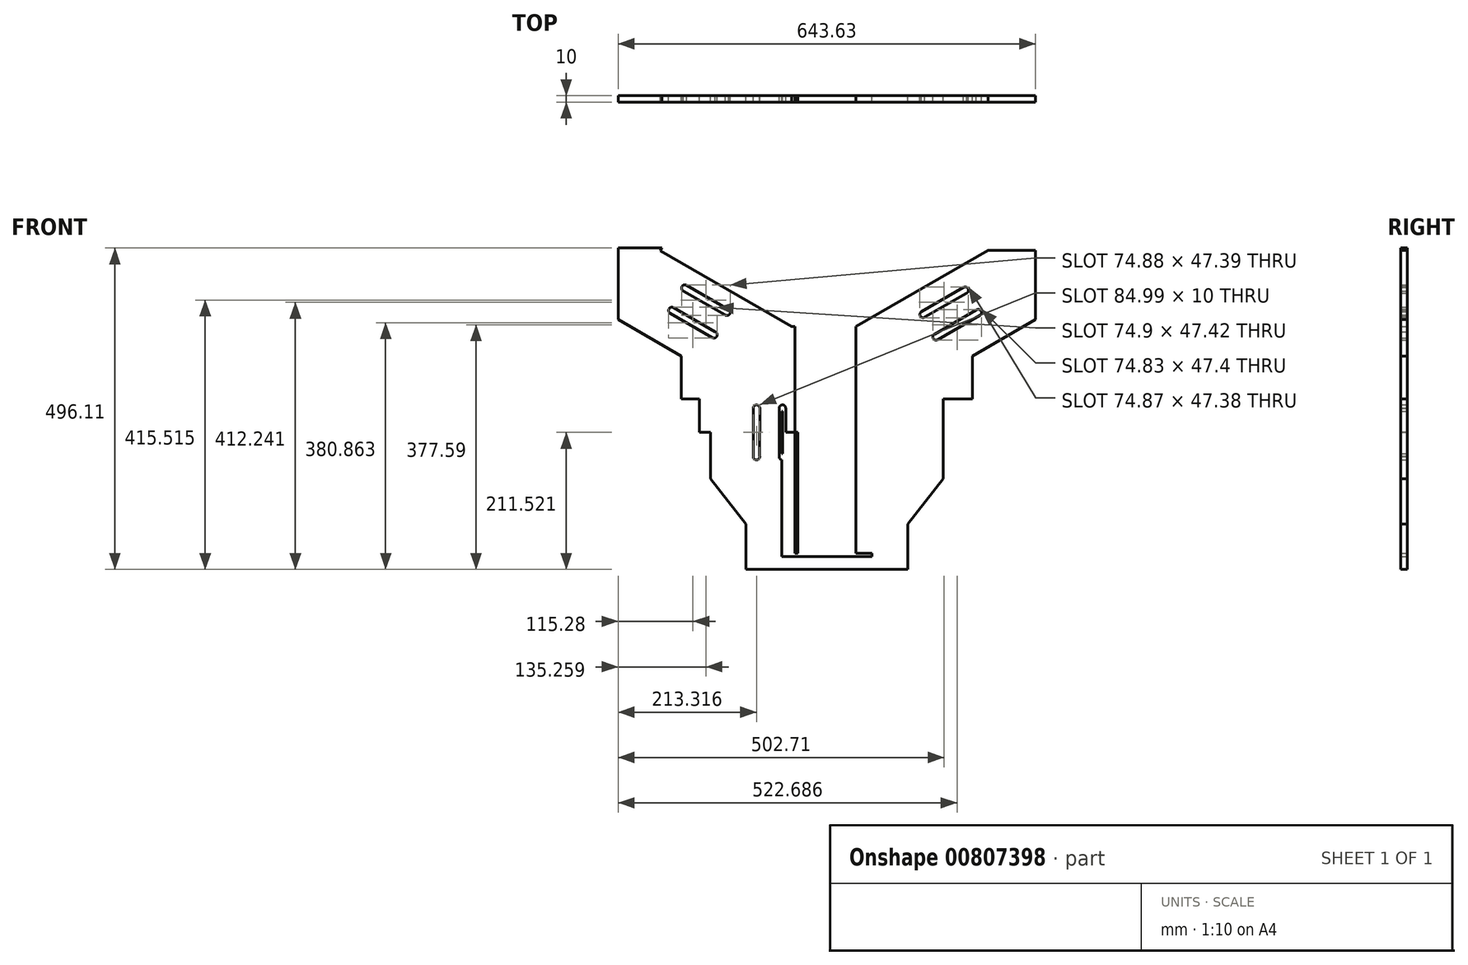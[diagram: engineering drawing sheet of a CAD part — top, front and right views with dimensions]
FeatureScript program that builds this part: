
annotation { "Feature Type Name" : "Feature", "Feature Type Description" : "" }
export const myFeature = defineFeature(function(context is Context, id is Id, definition is map)
    precondition{}
    {
        {
            var Q0;
            Q0=qCreatedBy(makeId("Front.planeOp"),FACE);
            var sketch = newSketch(context, id + "F0", { "sketchPlane" : qUnion([Q0])});
            skLineSegment(sketch, "E0", {"start": v(-67.46, 111.85) * mm, "end": v(-67.46, -238.15) * mm});
            skLineSegment(sketch, "E1", {"start": v(-67.46, -238.15) * mm, "end": v(-42.46, -238.15) * mm});
            skLineSegment(sketch, "E2", {"start": v(-42.46, -238.15) * mm, "end": v(-42.46, 111.85) * mm});
            skLineSegment(sketch, "E3", {"start": v(-42.46, 111.85) * mm, "end": v(-67.46, 111.85) * mm});
            skLineSegment(sketch, "E4", {"start": v(-42.46, 111.85) * mm, "end": v(-345.57, 286.85) * mm});
            skLineSegment(sketch, "E5", {"start": v(-345.57, 286.85) * mm, "end": v(-358.07, 265.2) * mm});
            skLineSegment(sketch, "E6", {"start": v(-358.07, 265.2) * mm, "end": v(-67.46, 97.42) * mm});
            skLineSegment(sketch, "E7", {"start": v(-67.46, -238.15) * mm, "end": v(-67.46, -263.15) * mm});
            skLineSegment(sketch, "E8", {"start": v(-67.46, -263.15) * mm, "end": v(71.54, -263.15) * mm});
            skLineSegment(sketch, "E9", {"start": v(71.54, -263.15) * mm, "end": v(71.54, -238.15) * mm});
            skLineSegment(sketch, "E10", {"start": v(71.54, -238.15) * mm, "end": v(-42.46, -238.15) * mm});
            skLineSegment(sketch, "E11", {"start": v(71.54, -238.15) * mm, "end": v(71.54, 111.85) * mm});
            skLineSegment(sketch, "E12", {"start": v(71.54, 111.85) * mm, "end": v(46.54, 111.85) * mm});
            skLineSegment(sketch, "E13", {"start": v(46.54, 111.85) * mm, "end": v(46.54, -238.15) * mm});
            skLineSegment(sketch, "E14", {"start": v(46.54, 111.85) * mm, "end": v(349.64, 286.85) * mm});
            skLineSegment(sketch, "E15", {"start": v(349.64, 286.85) * mm, "end": v(362.14, 265.2) * mm});
            skLineSegment(sketch, "E16", {"start": v(362.14, 265.2) * mm, "end": v(71.54, 97.42) * mm});
            skLineSegment(sketch, "E17", {"start": v(-345.57, 286.85) * mm, "end": v(-348.07, 282.52) * mm});
            skLineSegment(sketch, "E18", {"start": v(-348.07, 282.52) * mm, "end": v(-52.46, 111.85) * mm});
            skLineSegment(sketch, "E19", {"start": v(-42.46, 111.85) * mm, "end": v(-47.46, 111.85) * mm});
            skLineSegment(sketch, "E20", {"start": v(-47.46, 111.85) * mm, "end": v(-47.46, -238.15) * mm});
            skLineSegment(sketch, "E21", {"start": v(-67.46, -238.15) * mm, "end": v(-67.46, -243.15) * mm});
            skLineSegment(sketch, "E22", {"start": v(-67.46, -243.15) * mm, "end": v(71.54, -243.15) * mm});
            skLineSegment(sketch, "E23", {"start": v(46.54, -238.15) * mm, "end": v(51.54, -238.15) * mm});
            skLineSegment(sketch, "E24", {"start": v(51.54, -238.15) * mm, "end": v(51.54, 111.85) * mm});
            skPoint(sketch, "E24.endSnap0", {"position": v(59.04, 111.85) * mm});
            skLineSegment(sketch, "E25", {"start": v(349.64, 286.85) * mm, "end": v(352.14, 282.52) * mm});
            skLineSegment(sketch, "E26", {"start": v(352.14, 282.52) * mm, "end": v(56.54, 111.85) * mm});
            skLineSegment(sketch, "E27", {"start": v(-191.27, 155.1) * mm, "end": v(-243.23, 185.1) * mm});
            skLineSegment(sketch, "E28", {"start": v(-264.73, 197.63) * mm, "end": v(-319.78, 102.28) * mm});
            skLineSegment(sketch, "E29", {"start": v(-319.78, 102.28) * mm, "end": v(-67.46, -43.4) * mm});
            skLineSegment(sketch, "E30", {"start": v(-67.46, -18.3) * mm, "end": v(-67.46, -38.05) * mm});
            skLineSegment(sketch, "E31", {"start": v(-67.46, -38.05) * mm, "end": v(-67.46, -98.05) * mm});
            skLineSegment(sketch, "E32", {"start": v(-67.46, -123.15) * mm, "end": v(-177.46, -123.15) * mm});
            skLineSegment(sketch, "E33", {"start": v(-177.46, -123.15) * mm, "end": v(-177.46, 20.12) * mm});
            skLineSegment(sketch, "E34", {"start": v(-177.46, -123.15) * mm, "end": v(-67.46, -263.15) * mm});
            skLineSegment(sketch, "E35", {"start": v(71.54, -123.15) * mm, "end": v(181.54, -123.15) * mm});
            skLineSegment(sketch, "E36", {"start": v(181.54, -123.15) * mm, "end": v(71.54, -263.15) * mm});
            skLineSegment(sketch, "E37", {"start": v(181.54, -123.15) * mm, "end": v(181.54, 20.12) * mm});
            skLineSegment(sketch, "E38", {"start": v(71.54, -43.4) * mm, "end": v(181.54, 20.12) * mm});
            skLineSegment(sketch, "E39", {"start": v(181.54, 20.12) * mm, "end": v(323.85, 102.28) * mm});
            skLineSegment(sketch, "E40", {"start": v(323.85, 102.28) * mm, "end": v(262.88, 207.89) * mm});
            skLineSegment(sketch, "E41", {"start": v(-264.73, 211.3) * mm, "end": v(-252.23, 232.96) * mm});
            skLineSegment(sketch, "E42", {"start": v(262.88, 207.89) * mm, "end": v(250.38, 229.54) * mm});
            skLineSegment(sketch, "E43", {"start": v(-319.78, 102.28) * mm, "end": v(-319.78, 232.96) * mm});
            skLineSegment(sketch, "E44", {"start": v(-319.78, 232.96) * mm, "end": v(-252.23, 232.96) * mm});
            skLineSegment(sketch, "E45", {"start": v(250.38, 229.54) * mm, "end": v(323.85, 229.54) * mm});
            skLineSegment(sketch, "E46", {"start": v(323.85, 229.54) * mm, "end": v(323.85, 102.28) * mm});
            skLineSegment(sketch, "E47", {"start": v(-122.46, -193.15) * mm, "end": v(-122.46, -263.15) * mm});
            skLineSegment(sketch, "E48", {"start": v(-122.46, -263.15) * mm, "end": v(-67.46, -263.15) * mm});
            skLineSegment(sketch, "E49", {"start": v(71.54, -263.15) * mm, "end": v(126.54, -263.15) * mm});
            skPoint(sketch, "E49.endSnap0", {"position": v(126.54, -193.15) * mm});
            skLineSegment(sketch, "E50", {"start": v(126.54, -263.15) * mm, "end": v(126.54, -193.15) * mm});
            skLineSegment(sketch, "E51", {"start": v(-172.52, 173.14) * mm, "end": v(-222.52, 86.54) * mm});
            skLineSegment(sketch, "E52", {"start": v(-172.52, 173.14) * mm, "end": v(-183.27, 154.52) * mm});
            skLineSegment(sketch, "E53", {"start": v(-183.27, 154.52) * mm, "end": v(-215.74, 173.27) * mm});
            skLineSegment(sketch, "E54", {"start": v(-215.74, 173.27) * mm, "end": v(-217, 171.1) * mm});
            skLineSegment(sketch, "E55", {"start": v(-217, 171.1) * mm, "end": v(-152.04, 133.6) * mm});
            skCircle(sketch, "E56", {"center": v(-217, 171.1) * mm, "radius": 5 * mm});
            skCircle(sketch, "E57", {"center": v(-152.04, 133.6) * mm, "radius": 5 * mm});
            skLineSegment(sketch, "E58", {"start": v(-149.69, 138.02) * mm, "end": v(-154.4, 129.2) * mm});
            skLineSegment(sketch, "E59", {"start": v(-154.4, 129.2) * mm, "end": v(-219.64, 166.86) * mm});
            skLineSegment(sketch, "E60", {"start": v(-217, 171.1) * mm, "end": v(-237, 136.47) * mm});
            skLineSegment(sketch, "E61", {"start": v(-237, 136.47) * mm, "end": v(-172.04, 98.97) * mm});
            skCircle(sketch, "E62", {"center": v(-237, 136.47) * mm, "radius": 5 * mm});
            skCircle(sketch, "E63", {"center": v(-172.04, 98.97) * mm, "radius": 5 * mm});
            skLineSegment(sketch, "E64", {"start": v(-168.96, 102.9) * mm, "end": v(-234.5, 140.8) * mm});
            skLineSegment(sketch, "E65", {"start": v(-234.5, 140.8) * mm, "end": v(-239.5, 132.14) * mm});
            skLineSegment(sketch, "E66", {"start": v(-239.5, 132.14) * mm, "end": v(-174.54, 94.64) * mm});
            skLineSegment(sketch, "E67", {"start": v(-214.43, 175.4) * mm, "end": v(-149.69, 138.02) * mm});
            skLineSegment(sketch, "E68", {"start": v(-42.46, -51.64) * mm, "end": v(-63.96, -51.64) * mm});
            skLineSegment(sketch, "E69", {"start": v(-63.96, -51.64) * mm, "end": v(-63.96, -14.14) * mm});
            skLineSegment(sketch, "E70", {"start": v(-63.96, -14.14) * mm, "end": v(-66.46, -14.14) * mm});
            skLineSegment(sketch, "E71", {"start": v(-66.46, -14.14) * mm, "end": v(-66.46, -89.14) * mm});
            skCircle(sketch, "E72", {"center": v(-66.46, -14.14) * mm, "radius": 5 * mm});
            skCircle(sketch, "E73", {"center": v(-66.46, -89.14) * mm, "radius": 5 * mm});
            skLineSegment(sketch, "E74", {"start": v(-61.47, -88.97) * mm, "end": v(-71.46, -89.3) * mm});
            skLineSegment(sketch, "E75", {"start": v(-71.46, -89.3) * mm, "end": v(-71.46, -13.97) * mm});
            skLineSegment(sketch, "E76", {"start": v(-66.46, -14.14) * mm, "end": v(-106.46, -14.14) * mm});
            skLineSegment(sketch, "E77", {"start": v(-106.46, -14.14) * mm, "end": v(-106.46, -89.14) * mm});
            skCircle(sketch, "E78", {"center": v(-106.46, -14.14) * mm, "radius": 5 * mm});
            skCircle(sketch, "E79", {"center": v(-106.46, -89.14) * mm, "radius": 5 * mm});
            skLineSegment(sketch, "E80", {"start": v(-101.51, -89.83) * mm, "end": v(-101.46, -14.14) * mm});
            skLineSegment(sketch, "E81", {"start": v(-101.46, -14.14) * mm, "end": v(-111.46, -14.14) * mm});
            skLineSegment(sketch, "E82", {"start": v(-111.46, -14.14) * mm, "end": v(-111.46, -89.14) * mm});
            skLineSegment(sketch, "E83", {"start": v(-61.46, -14.21) * mm, "end": v(-61.47, -88.97) * mm});
            skLineSegment(sketch, "E84", {"start": v(170.93, 169.87) * mm, "end": v(181.68, 151.26) * mm});
            skLineSegment(sketch, "E85", {"start": v(181.68, 151.26) * mm, "end": v(149.2, 132.5) * mm});
            skLineSegment(sketch, "E86", {"start": v(149.2, 132.5) * mm, "end": v(150.45, 130.34) * mm});
            skLineSegment(sketch, "E87", {"start": v(150.45, 130.34) * mm, "end": v(215.4, 167.84) * mm});
            skCircle(sketch, "E88", {"center": v(150.45, 130.34) * mm, "radius": 5 * mm});
            skCircle(sketch, "E89", {"center": v(215.4, 167.84) * mm, "radius": 5 * mm});
            skLineSegment(sketch, "E90", {"start": v(212.76, 172.08) * mm, "end": v(218.05, 163.6) * mm});
            skLineSegment(sketch, "E91", {"start": v(218.05, 163.6) * mm, "end": v(152.8, 125.93) * mm});
            skLineSegment(sketch, "E92", {"start": v(150.45, 130.34) * mm, "end": v(170.45, 95.7) * mm});
            skLineSegment(sketch, "E93", {"start": v(170.45, 95.7) * mm, "end": v(235.4, 133.2) * mm});
            skCircle(sketch, "E94", {"center": v(170.45, 95.7) * mm, "radius": 5 * mm});
            skCircle(sketch, "E95", {"center": v(235.4, 133.2) * mm, "radius": 5 * mm});
            skLineSegment(sketch, "E96", {"start": v(233.53, 137.84) * mm, "end": v(167.95, 100.03) * mm});
            skLineSegment(sketch, "E97", {"start": v(167.95, 100.03) * mm, "end": v(172.95, 91.37) * mm});
            skLineSegment(sketch, "E98", {"start": v(172.95, 91.37) * mm, "end": v(237.9, 128.87) * mm});
            skLineSegment(sketch, "E99", {"start": v(148.02, 134.7) * mm, "end": v(212.76, 172.08) * mm});
            skLineSegment(sketch, "E100", {"start": v(170.93, 169.87) * mm, "end": v(144.01, 154.34) * mm});
            skLineSegment(sketch, "E101", {"start": v(-172.52, 173.14) * mm, "end": v(-150.87, 160.64) * mm});
            skLineSegment(sketch, "E102", {"start": v(-42.46, -51.64) * mm, "end": v(-42.46, -26.64) * mm});
            skLineSegment(sketch, "E103", {"start": v(-222.52, 86.54) * mm, "end": v(-222.52, 0) * mm});
            skLineSegment(sketch, "E104", {"start": v(-222.52, 0) * mm, "end": v(-177.46, 0) * mm});
            skLineSegment(sketch, "E105", {"start": v(181.54, 0) * mm, "end": v(226.6, 0) * mm});
            skLineSegment(sketch, "E106", {"start": v(226.6, 0) * mm, "end": v(226.6, 46.13) * mm});
            skLineSegment(sketch, "E107", {"start": v(-222.52, 46.13) * mm, "end": v(-222.52, 66.13) * mm});
            skLineSegment(sketch, "E108", {"start": v(226.6, 46.13) * mm, "end": v(226.6, 66.13) * mm});
            skLineSegment(sketch, "E109", {"start": v(226.6, 66.13) * mm, "end": v(323.85, 122.28) * mm});
            skLineSegment(sketch, "E110", {"start": v(-222.52, 66.13) * mm, "end": v(-319.78, 122.28) * mm});
            skLineSegment(sketch, "E111", {"start": v(-177.46, -51.52) * mm, "end": v(-194.72, -51.52) * mm});
            skLineSegment(sketch, "E112", {"start": v(-194.72, -51.52) * mm, "end": v(-194.72, 0) * mm});
            skSolve(sketch);
        }
        {
            var Q0;
            {var subQ0=sQuery(id+"F0.wireOp",EDGE,"E41");var subQ1=sQuery(id+"F0.wireOp",EDGE,"E6");var subQ2=makeQuery(id+"F0.imprint","INTERSECT",VERTEX,{"derivedFrom":[subQ1,subQ0]});Q0=makeQuery(id+"F0.imprint","IMPRINT",FACE,{"disambiguationData":[TD([[makeQuery(id+"F0.imprint","IMPRINT",EDGE,{"disambiguationData":[TD([[subQ2,1.0]])],"derivedFrom":subQ1}),1.0]])]});}
            var Q1;
            {var subQ0=sQuery(id+"F0.wireOp",EDGE,"E19");Q1=makeQuery(id+"F0.imprint","IMPRINT",FACE,{"disambiguationData":[TD([[makeQuery(id+"F0.imprint","IMPRINT",EDGE,{"derivedFrom":subQ0}),-1.0]])]});}
            var Q2;
            {var subQ0=sQuery(id+"F0.wireOp",EDGE,"E6");var subQ3=makeQuery(id+"F0.imprint","IMPRINT",VERTEX,{"derivedFrom":subQ0});Q2=makeQuery(id+"F0.imprint","IMPRINT",FACE,{"disambiguationData":[TD([[makeQuery(id+"F0.imprint","IMPRINT",EDGE,{"disambiguationData":[TD([[subQ3,1.0]])],"derivedFrom":subQ0}),1.0]])]});}
            var Q3;
            {var subQ5=sQuery(id+"F0.wireOp",EDGE,"E19");Q3=makeQuery(id+"F0.imprint","IMPRINT",FACE,{"disambiguationData":[TD([[makeQuery(id+"F0.imprint","IMPRINT",EDGE,{"derivedFrom":subQ5}),1.0]])]});}
            var Q4;
            {var subQ1=sQuery(id+"F0.wireOp",EDGE,"E7");Q4=makeQuery(id+"F0.imprint","IMPRINT",FACE,{"disambiguationData":[TD([[makeQuery(id+"F0.imprint","IMPRINT",EDGE,{"derivedFrom":subQ1}),-1.0]])]});}
            var Q5;
            {var subQ1=sQuery(id+"F0.wireOp",EDGE,"E1");var subQ3=sQuery(id+"F0.wireOp",EDGE,"E20");var subQ4=makeQuery(id+"F0.imprint","INTERSECT",VERTEX,{"derivedFrom":[subQ1,subQ3]});Q5=makeQuery(id+"F0.imprint","IMPRINT",FACE,{"disambiguationData":[TD([[makeQuery(id+"F0.imprint","IMPRINT",EDGE,{"disambiguationData":[TD([[subQ4,1.0]])],"derivedFrom":subQ3}),1.0]])]});}
            var Q6;
            {var subQ2=sQuery(id+"F0.wireOp",EDGE,"E47");Q6=makeQuery(id+"F0.imprint","IMPRINT",FACE,{"disambiguationData":[TD([[makeQuery(id+"F0.imprint","IMPRINT",EDGE,{"derivedFrom":subQ2}),1.0]])]});}
            var Q7;
            Q7=makeQuery(id+"F0.imprint","IMPRINT",FACE,{"disambiguationData":[TD([[makeQuery(id+"F0.imprint","IMPRINT",EDGE,{"derivedFrom":sQuery(id+"F0.wireOp",EDGE,"E7")}),1.0]])]});
            var Q8;
            {var subQ8=sQuery(id+"F0.wireOp",EDGE,"E21");Q8=makeQuery(id+"F0.imprint","IMPRINT",FACE,{"disambiguationData":[TD([[makeQuery(id+"F0.imprint","IMPRINT",EDGE,{"derivedFrom":subQ8}),1.0]])]});}
            var Q9;
            {var subQ0=sQuery(id+"F0.wireOp",EDGE,"E49");Q9=makeQuery(id+"F0.imprint","IMPRINT",FACE,{"disambiguationData":[TD([[makeQuery(id+"F0.imprint","IMPRINT",EDGE,{"derivedFrom":subQ0}),1.0]])]});}
            var Q10;
            {var subQ0=sQuery(id+"F0.wireOp",EDGE,"E35");Q10=makeQuery(id+"F0.imprint","IMPRINT",FACE,{"disambiguationData":[TD([[makeQuery(id+"F0.imprint","IMPRINT",EDGE,{"derivedFrom":subQ0}),-1.0]])]});}
            var Q11;
            {var subQ6=sQuery(id+"F0.wireOp",EDGE,"E24");Q11=makeQuery(id+"F0.imprint","IMPRINT",FACE,{"disambiguationData":[TD([[makeQuery(id+"F0.imprint","IMPRINT",EDGE,{"derivedFrom":subQ6}),-1.0]])]});}
            var Q12;
            {var subQ0=sQuery(id+"F0.wireOp",EDGE,"E13");Q12=makeQuery(id+"F0.imprint","IMPRINT",FACE,{"disambiguationData":[TD([[makeQuery(id+"F0.imprint","IMPRINT",EDGE,{"derivedFrom":subQ0}),1.0]])]});}
            var Q13;
            {var subQ8=sQuery(id+"F0.wireOp",EDGE,"E38");Q13=makeQuery(id+"F0.imprint","IMPRINT",FACE,{"disambiguationData":[TD([[makeQuery(id+"F0.imprint","IMPRINT",EDGE,{"derivedFrom":subQ8}),1.0]])]});}
            var Q14;
            {var subQ0=sQuery(id+"F0.wireOp",EDGE,"E35");Q14=makeQuery(id+"F0.imprint","IMPRINT",FACE,{"disambiguationData":[TD([[makeQuery(id+"F0.imprint","IMPRINT",EDGE,{"derivedFrom":subQ0}),1.0]])]});}
            var Q15;
            {var subQ0=sQuery(id+"F0.wireOp",EDGE,"E16");var subQ3=makeQuery(id+"F0.imprint","IMPRINT",VERTEX,{"derivedFrom":subQ0});Q15=makeQuery(id+"F0.imprint","IMPRINT",FACE,{"disambiguationData":[TD([[makeQuery(id+"F0.imprint","IMPRINT",EDGE,{"disambiguationData":[TD([[subQ3,-1.0]])],"derivedFrom":subQ0}),-1.0]])]});}
            var Q16;
            {var subQ1=sQuery(id+"F0.wireOp",EDGE,"E12");var subQ8=makeQuery(id+"F0.imprint","INTERSECT",VERTEX,{"derivedFrom":[subQ1,sQuery(id+"F0.wireOp",EDGE,"E24")]});Q16=makeQuery(id+"F0.imprint","IMPRINT",FACE,{"disambiguationData":[TD([[makeQuery(id+"F0.imprint","IMPRINT",EDGE,{"disambiguationData":[TD([[subQ8,1.0]])],"derivedFrom":subQ1}),-1.0]])]});}
            var Q17;
            {var subQ3=sQuery(id+"F0.wireOp",EDGE,"E45");var subQ5=sQuery(id+"F0.wireOp",EDGE,"E26");var subQ6=makeQuery(id+"F0.imprint","INTERSECT",VERTEX,{"derivedFrom":[subQ5,subQ3]});Q17=makeQuery(id+"F0.imprint","IMPRINT",FACE,{"disambiguationData":[TD([[makeQuery(id+"F0.imprint","IMPRINT",EDGE,{"disambiguationData":[TD([[subQ6,-1.0]])],"derivedFrom":subQ5}),1.0]])]});}
            var Q18;
            {var subQ0=sQuery(id+"F0.wireOp",EDGE,"E45");var subQ1=sQuery(id+"F0.wireOp",EDGE,"E26");var subQ2=makeQuery(id+"F0.imprint","INTERSECT",VERTEX,{"derivedFrom":[subQ1,subQ0]});Q18=makeQuery(id+"F0.imprint","IMPRINT",FACE,{"disambiguationData":[TD([[makeQuery(id+"F0.imprint","IMPRINT",EDGE,{"disambiguationData":[TD([[subQ2,-1.0]])],"derivedFrom":subQ1}),-1.0]])]});}
            var Q19;
            {var subQ0=sQuery(id+"F0.wireOp",EDGE,"E44");var subQ1=sQuery(id+"F0.wireOp",EDGE,"E18");var subQ2=makeQuery(id+"F0.imprint","INTERSECT",VERTEX,{"derivedFrom":[subQ1,subQ0]});Q19=makeQuery(id+"F0.imprint","IMPRINT",FACE,{"disambiguationData":[TD([[makeQuery(id+"F0.imprint","IMPRINT",EDGE,{"disambiguationData":[TD([[subQ2,-1.0]])],"derivedFrom":subQ1}),1.0]])]});}
            var Q20;
            {var subQ5=sQuery(id+"F0.wireOp",EDGE,"E59");var subQ6=sQuery(id+"F0.wireOp",EDGE,"E51");var subQ7=makeQuery(id+"F0.imprint","INTERSECT",VERTEX,{"derivedFrom":[subQ6,subQ5]});Q20=makeQuery(id+"F0.imprint","IMPRINT",FACE,{"disambiguationData":[TD([[makeQuery(id+"F0.imprint","IMPRINT",EDGE,{"disambiguationData":[TD([[subQ7,-1.0]])],"derivedFrom":subQ6}),-1.0]])]});}
            var Q21;
            {var subQ15=sQuery(id+"F0.wireOp",EDGE,"E32");Q21=makeQuery(id+"F0.imprint","IMPRINT",FACE,{"disambiguationData":[TD([[makeQuery(id+"F0.imprint","IMPRINT",EDGE,{"derivedFrom":subQ15}),-1.0]])]});}
            var Q22;
            {var subQ0=sQuery(id+"F0.wireOp",EDGE,"E3");var subQ1=sQuery(id+"F0.wireOp",EDGE,"E0");var subQ2=makeQuery(id+"F0.imprint","INTERSECT",VERTEX,{"derivedFrom":[subQ1,subQ0]});Q22=makeQuery(id+"F0.imprint","IMPRINT",FACE,{"disambiguationData":[TD([[makeQuery(id+"F0.imprint","IMPRINT",EDGE,{"disambiguationData":[TD([[subQ2,-1.0]])],"derivedFrom":subQ1}),1.0]])]});}
            var Q23;
            {var subQ5=sQuery(id+"F0.wireOp",EDGE,"E0");var subQ8=sQuery(id+"F0.wireOp",EDGE,"E31");var subQ9=makeQuery(id+"F0.imprint","INTERSECT",VERTEX,{"derivedFrom":[subQ5,subQ8]});Q23=makeQuery(id+"F0.imprint","IMPRINT",FACE,{"disambiguationData":[TD([[makeQuery(id+"F0.imprint","IMPRINT",EDGE,{"disambiguationData":[TD([[subQ9,-1.0]])],"derivedFrom":subQ5}),1.0]])]});}
            var Q24;
            {var subQ6=sQuery(id+"F0.wireOp",EDGE,"E29");var subQ9=sQuery(id+"F0.wireOp",EDGE,"E80");var subQ10=makeQuery(id+"F0.imprint","INTERSECT",VERTEX,{"derivedFrom":[subQ6,subQ9]});Q24=makeQuery(id+"F0.imprint","IMPRINT",FACE,{"disambiguationData":[TD([[makeQuery(id+"F0.imprint","IMPRINT",EDGE,{"disambiguationData":[TD([[subQ10,-1.0]])],"derivedFrom":subQ6}),1.0]])]});}
            var Q25;
            {var subQ20=sQuery(id+"F0.wireOp",EDGE,"E6");var subQ23=sQuery(id+"F0.wireOp",EDGE,"E0");var subQ24=makeQuery(id+"F0.imprint","INTERSECT",VERTEX,{"derivedFrom":[subQ23,subQ20]});Q25=makeQuery(id+"F0.imprint","IMPRINT",FACE,{"disambiguationData":[TD([[makeQuery(id+"F0.imprint","IMPRINT",EDGE,{"disambiguationData":[TD([[subQ24,-1.0]])],"derivedFrom":subQ23}),-1.0]])]});}
            var Q26;
            {var subQ5=sQuery(id+"F0.wireOp",EDGE,"E104");Q26=makeQuery(id+"F0.imprint","IMPRINT",FACE,{"disambiguationData":[TD([[makeQuery(id+"F0.imprint","IMPRINT",EDGE,{"derivedFrom":subQ5}),1.0]])]});}
            var Q27;
            {var subQ1=sQuery(id+"F0.wireOp",EDGE,"E0");var subQ6=sQuery(id+"F0.wireOp",EDGE,"E3");var subQ7=makeQuery(id+"F0.imprint","INTERSECT",VERTEX,{"derivedFrom":[subQ1,subQ6]});Q27=makeQuery(id+"F0.imprint","IMPRINT",FACE,{"disambiguationData":[TD([[makeQuery(id+"F0.imprint","IMPRINT",EDGE,{"disambiguationData":[TD([[subQ7,-1.0]])],"derivedFrom":subQ1}),-1.0]])]});}
            var Q28;
            {var subQ3=sQuery(id+"F0.wireOp",EDGE,"E105");Q28=makeQuery(id+"F0.imprint","IMPRINT",FACE,{"disambiguationData":[TD([[makeQuery(id+"F0.imprint","IMPRINT",EDGE,{"derivedFrom":subQ3}),1.0]])]});}
            var Q29;
            {var subQ0=sQuery(id+"F0.wireOp",EDGE,"E46");var subQ1=sQuery(id+"F0.wireOp",EDGE,"E45");var subQ2=makeQuery(id+"F0.imprint","INTERSECT",VERTEX,{"derivedFrom":[subQ1,subQ0]});Q29=makeQuery(id+"F0.imprint","IMPRINT",FACE,{"disambiguationData":[TD([[makeQuery(id+"F0.imprint","IMPRINT",EDGE,{"disambiguationData":[TD([[subQ2,1.0]])],"derivedFrom":subQ1}),-1.0]])]});}
            var Q30;
            {var subQ14=sQuery(id+"F0.wireOp",EDGE,"E6");var subQ24=makeQuery(id+"F0.imprint","INTERSECT",VERTEX,{"derivedFrom":[subQ14,sQuery(id+"F0.wireOp",EDGE,"E41")]});Q30=makeQuery(id+"F0.imprint","IMPRINT",FACE,{"disambiguationData":[TD([[makeQuery(id+"F0.imprint","IMPRINT",EDGE,{"disambiguationData":[TD([[subQ24,1.0]])],"derivedFrom":subQ14}),-1.0]])]});}
            var Q31;
            {var subQ3=sQuery(id+"F0.wireOp",EDGE,"E111");Q31=makeQuery(id+"F0.imprint","IMPRINT",FACE,{"disambiguationData":[TD([[makeQuery(id+"F0.imprint","IMPRINT",EDGE,{"derivedFrom":subQ3}),-1.0]])]});}
            extrude(context, id + "F1", {"entities" : qUnion([Q0, Q1, Q2, Q3, Q4, Q5, Q6, Q7, Q8, Q9, Q10, Q11, Q12, Q13, Q14, Q15, Q16, Q17, Q18, Q19, Q20, Q21, Q22, Q23, Q24, Q25, Q26, Q27, Q28, Q29, Q30, Q31]), "depth" : 10 * mm, "offsetDistance" : 25 * mm});
        }
    });
